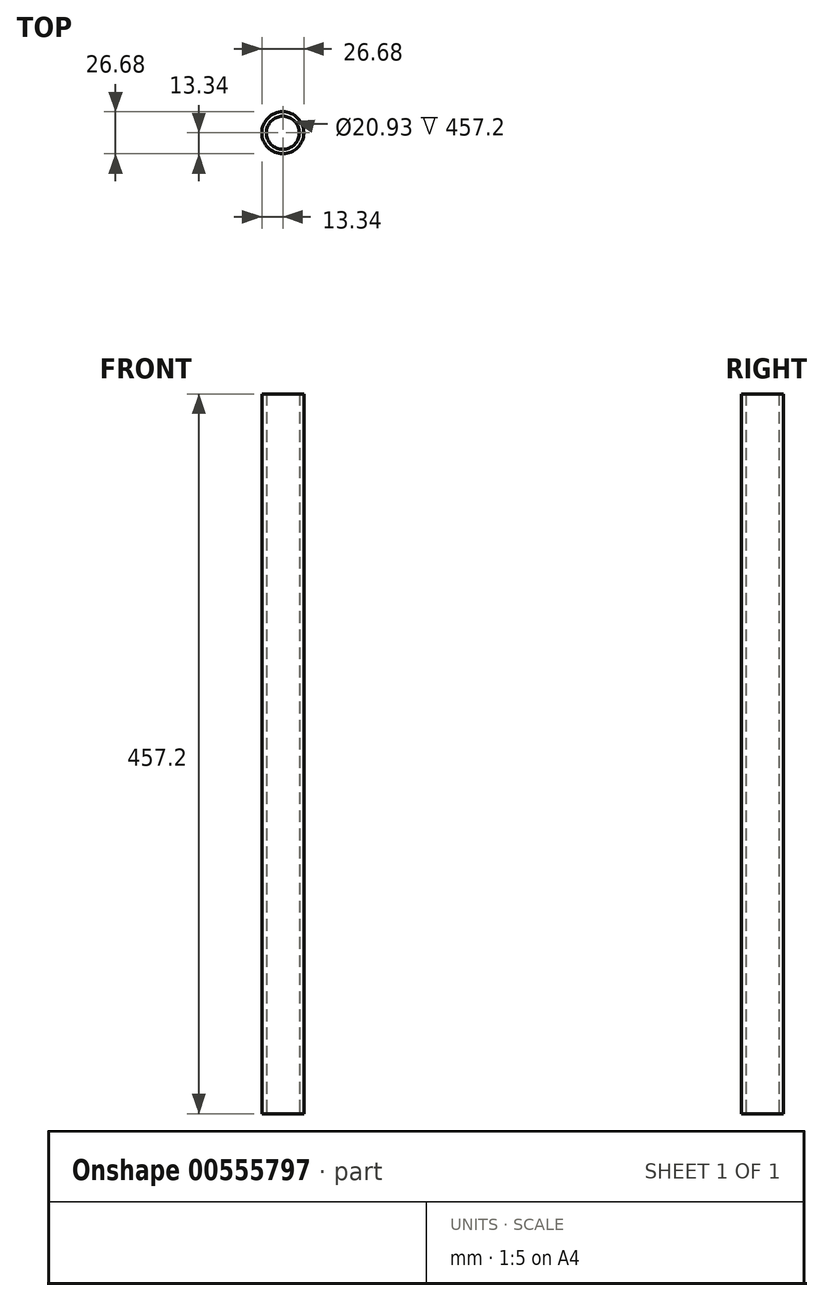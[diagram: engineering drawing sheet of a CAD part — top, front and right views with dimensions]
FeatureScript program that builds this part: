
annotation { "Feature Type Name" : "Feature", "Feature Type Description" : "" }
export const myFeature = defineFeature(function(context is Context, id is Id, definition is map)
    precondition{}
    {
        {
            var Q0;
            Q0=qCreatedBy(makeId("Top.planeOp"),FACE);
            var sketch = newSketch(context, id + "F0", { "sketchPlane" : qUnion([Q0])});
            skCircle(sketch, "E0", {"center": v(0, 0) * mm, "radius": 13.33 * mm});
            skCircle(sketch, "E1", {"center": v(0, 0) * mm, "radius": 10.46 * mm});
            skSolve(sketch);
        }
        {
            var Q0;
            Q0=qSketchRegion(id+"F0",true);
            extrude(context, id + "F1", {"entities" : qUnion([Q0]), "depth" : 457.2 * mm, "offsetDistance" : 25.4 * mm});
        }
    });
